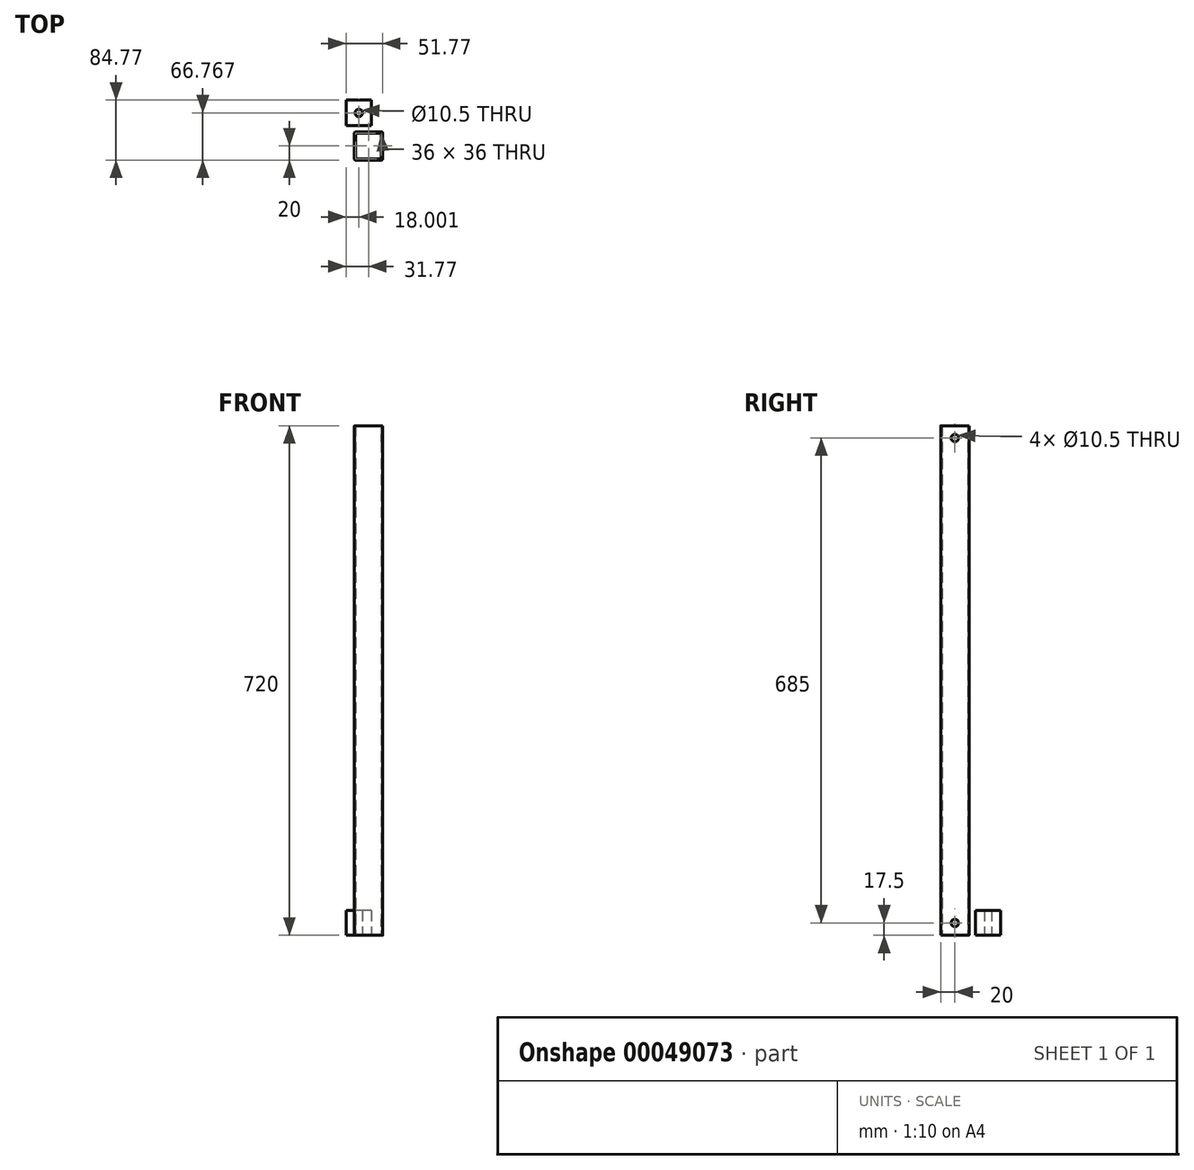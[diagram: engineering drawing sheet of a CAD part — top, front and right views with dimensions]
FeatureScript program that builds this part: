
annotation { "Feature Type Name" : "Feature", "Feature Type Description" : "" }
export const myFeature = defineFeature(function(context is Context, id is Id, definition is map)
    precondition{}
    {
        {
            var Q0;
            Q0=qCreatedBy(makeId("Top.planeOp"),FACE);
            var sketch = newSketch(context, id + "F0", { "sketchPlane" : qUnion([Q0])});
            skLineSegment(sketch, "E0.bottom", {"start": v(0, 0) * mm, "end": v(-40, 0) * mm});
            skLineSegment(sketch, "E0.top", {"start": v(0, -40) * mm, "end": v(-40, -40) * mm});
            skLineSegment(sketch, "E0.left", {"start": v(0, 0) * mm, "end": v(0, -40) * mm});
            skLineSegment(sketch, "E0.right", {"start": v(-40, 0) * mm, "end": v(-40, -40) * mm});
            skLineSegment(sketch, "E1.0", {"start": v(-2, -2) * mm, "end": v(-38, -2) * mm});
            skLineSegment(sketch, "E1.1", {"start": v(-2, -2) * mm, "end": v(-2, -38) * mm});
            skLineSegment(sketch, "E1.2", {"start": v(-2, -38) * mm, "end": v(-38, -38) * mm});
            skLineSegment(sketch, "E1.3", {"start": v(-38, -2) * mm, "end": v(-38, -38) * mm});
            skSolve(sketch);
        }
        {
            var Q0;
            Q0 = qSketchRegion(id + "F0", true);
            extrude(context, id + "F1", {"entities" : qUnion([Q0]), "depth" : 720 * mm});
        }
        {
            var Q0;
            Q0=qCreatedBy(makeId("Top.planeOp"),FACE);
            var sketch = newSketch(context, id + "F2", { "sketchPlane" : qUnion([Q0])});
            skLineSegment(sketch, "E2.bottom", {"start": v(-15.77, 8.77) * mm, "end": v(-51.77, 8.77) * mm});
            skLineSegment(sketch, "E2.top", {"start": v(-15.77, 44.77) * mm, "end": v(-51.77, 44.77) * mm});
            skLineSegment(sketch, "E2.left", {"start": v(-15.77, 8.77) * mm, "end": v(-15.77, 44.77) * mm});
            skLineSegment(sketch, "E2.right", {"start": v(-51.77, 8.77) * mm, "end": v(-51.77, 44.77) * mm});
            skCircle(sketch, "E3", {"center": v(-33.77, 26.77) * mm, "radius": 5.25 * mm});
            skPoint(sketch, "E3.centerSnap0", {"position": v(-51.77, 26.77) * mm});
            skPoint(sketch, "E3.centerSnap1", {"position": v(-33.77, 8.77) * mm});
            skSolve(sketch);
        }
        {
            var Q0;
            Q0 = qSketchRegion(id + "F2", true);
            extrude(context, id + "F3", {"entities" : qUnion([Q0]), "depth" : 35 * mm});
        }
        {
            var Q0;
            Q0=makeQuery(id+"F1.opExtrude","SWEPT_FACE",FACE,{"disambiguationData":[OSD([sQuery(id+"F0.wireOp",EDGE,"E0.right")])]});
            var sketch = newSketch(context, id + "F4", { "sketchPlane" : qUnion([Q0])});
            skLineSegment(sketch, "E4", {"start": v(40, 0) * mm, "end": v(0, 0) * mm});
            skLineSegment(sketch, "E5", {"start": v(40, 17.5) * mm, "end": v(0, 17.5) * mm});
            skCircle(sketch, "E6", {"center": v(20, 17.5) * mm, "radius": 5.25 * mm});
            skSolve(sketch);
        }
        {
            var Q0;
            Q0=sQuery(id+"F4.wireOp",VERTEX,"E6.center");
            var Q1;
            Q1=makeQuery(id+"F1.opExtrude","SWEPT_BODY",BODY,{"disambiguationData":[OSD([sQuery(id+"F0.wireOp",EDGE,"E0.bottom"),sQuery(id+"F0.wireOp",EDGE,"E0.top"),sQuery(id+"F0.wireOp",EDGE,"E0.left"),sQuery(id+"F0.wireOp",EDGE,"E0.right"),sQuery(id+"F0.wireOp",EDGE,"E1.0"),sQuery(id+"F0.wireOp",EDGE,"E1.1"),sQuery(id+"F0.wireOp",EDGE,"E1.2"),sQuery(id+"F0.wireOp",EDGE,"E1.3")])]});
            hole(context, id + "F5", {"style" : HoleStyle.SIMPLE, "holeDiameter" : 10.5 * mm, "endStyle" : HoleEndStyle.THROUGH, "locations" : qUnion([Q0]), "scope" : qUnion([Q1])});
        }
        {
            var Q0;
            Q0=makeQuery(id+"F1.opExtrude","SWEPT_FACE",FACE,{"disambiguationData":[OSD([sQuery(id+"F0.wireOp",EDGE,"E0.right")])]});
            var sketch = newSketch(context, id + "F6", { "sketchPlane" : qUnion([Q0])});
            skLineSegment(sketch, "E7", {"start": v(40, 720) * mm, "end": v(0, 720) * mm});
            skLineSegment(sketch, "E8", {"start": v(40, 702.5) * mm, "end": v(0, 702.5) * mm});
            skCircle(sketch, "E9", {"center": v(20, 702.5) * mm, "radius": 5.25 * mm});
            skSolve(sketch);
        }
        {
            var Q0;
            Q0=sQuery(id+"F6.wireOp",VERTEX,"E9.center");
            var Q1;
            Q1=makeQuery(id+"F1.opExtrude","SWEPT_BODY",BODY,{"disambiguationData":[OSD([sQuery(id+"F0.wireOp",EDGE,"E0.bottom"),sQuery(id+"F0.wireOp",EDGE,"E0.top"),sQuery(id+"F0.wireOp",EDGE,"E0.left"),sQuery(id+"F0.wireOp",EDGE,"E0.right"),sQuery(id+"F0.wireOp",EDGE,"E1.0"),sQuery(id+"F0.wireOp",EDGE,"E1.1"),sQuery(id+"F0.wireOp",EDGE,"E1.2"),sQuery(id+"F0.wireOp",EDGE,"E1.3")])]});
            hole(context, id + "F7", {"style" : HoleStyle.SIMPLE, "holeDiameter" : 10.5 * mm, "endStyle" : HoleEndStyle.THROUGH, "locations" : qUnion([Q0]), "scope" : qUnion([Q1])});
        }
        {
            var Q0;
            Q0=makeQuery(id+"F1.opExtrude","SWEPT_EDGE",EDGE,{"disambiguationData":[OSD([sQuery(id+"F0.wireOp",EDGE,"E0.top"),sQuery(id+"F0.wireOp",EDGE,"E0.left")])]});
            var Q1;
            Q1=makeQuery(id+"F1.opExtrude","SWEPT_EDGE",EDGE,{"disambiguationData":[OSD([sQuery(id+"F0.wireOp",EDGE,"E0.bottom"),sQuery(id+"F0.wireOp",EDGE,"E0.left")])]});
            var Q2;
            Q2=makeQuery(id+"F1.opExtrude","SWEPT_EDGE",EDGE,{"disambiguationData":[OSD([sQuery(id+"F0.wireOp",EDGE,"E0.top"),sQuery(id+"F0.wireOp",EDGE,"E0.right")])]});
            var Q3;
            Q3=makeQuery(id+"F1.opExtrude","SWEPT_EDGE",EDGE,{"disambiguationData":[OSD([sQuery(id+"F0.wireOp",EDGE,"E0.bottom"),sQuery(id+"F0.wireOp",EDGE,"E0.right")])]});
            fillet(context, id + "F8", {"entities" : qUnion([Q0, Q1, Q2, Q3]), "radius" : 2 * mm, "tangentPropagation" : true, "allowEdgeOverflow" : false});
        }
    });
